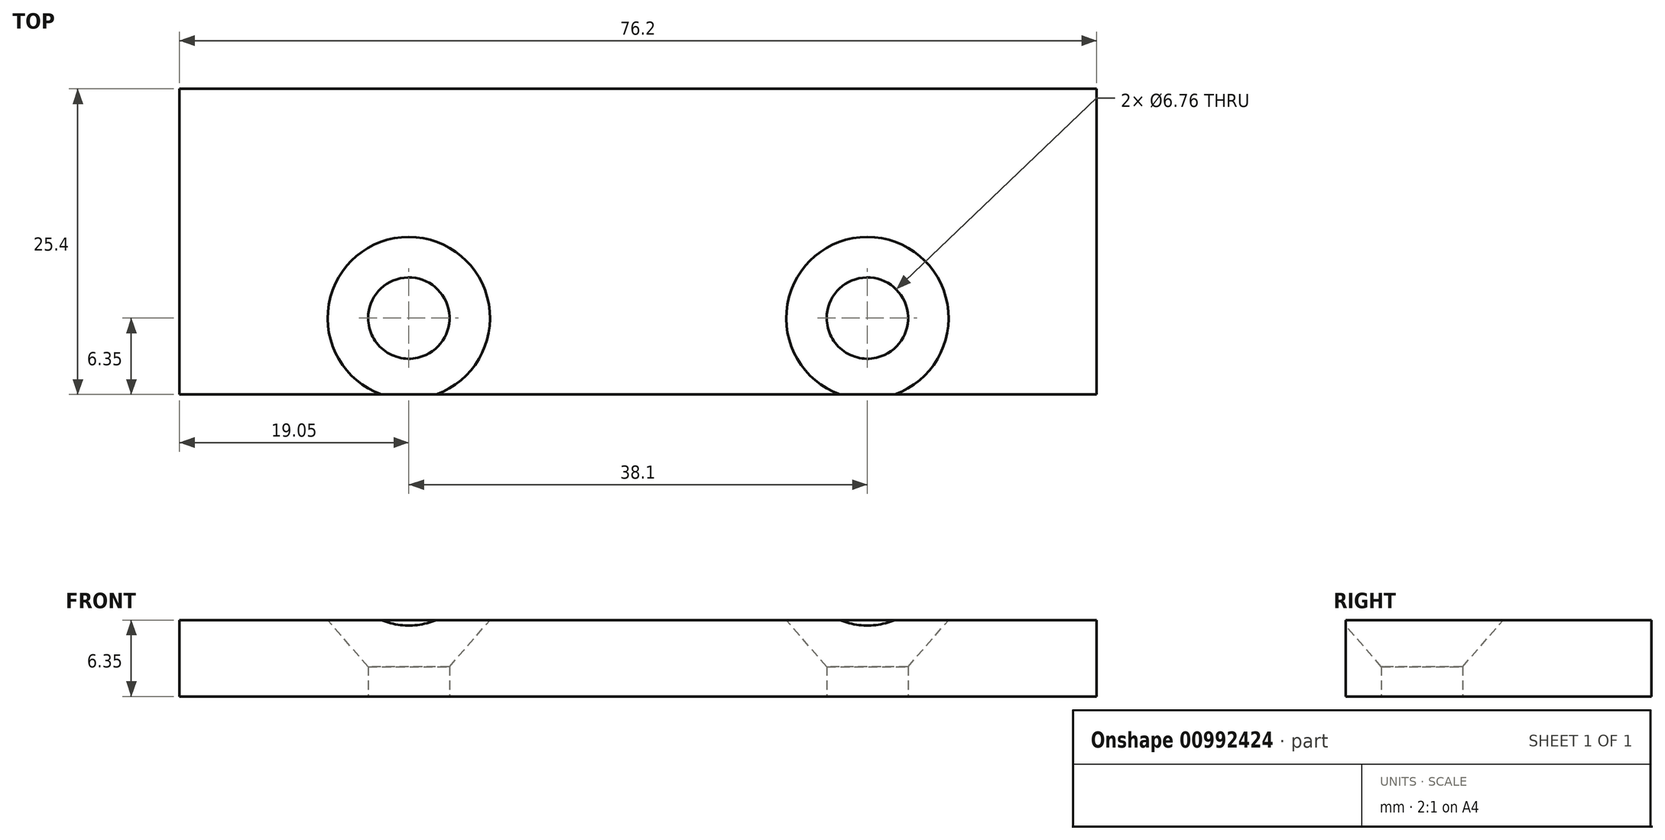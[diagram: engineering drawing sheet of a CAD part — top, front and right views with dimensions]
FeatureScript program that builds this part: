
annotation { "Feature Type Name" : "Feature", "Feature Type Description" : "" }
export const myFeature = defineFeature(function(context is Context, id is Id, definition is map)
    precondition{}
    {
        {
            var Q0;
            Q0=qCreatedBy(makeId("Top.planeOp"),FACE);
            var sketch = newSketch(context, id + "F0", { "sketchPlane" : qUnion([Q0])});
            skLineSegment(sketch, "E0.bottom", {"start": v(38.1, 12.7) * mm, "end": v(-38.1, 12.7) * mm});
            skLineSegment(sketch, "E0.top", {"start": v(38.1, -12.7) * mm, "end": v(-38.1, -12.7) * mm});
            skLineSegment(sketch, "E0.left", {"start": v(38.1, 12.7) * mm, "end": v(38.1, -12.7) * mm});
            skLineSegment(sketch, "E0.right", {"start": v(-38.1, 12.7) * mm, "end": v(-38.1, -12.7) * mm});
            skPoint(sketch, "E0.middle", {"position": v(0, 0) * mm});
            skCircle(sketch, "E1", {"center": v(-19.05, -6.35) * mm, "radius": 3.57 * mm});
            skCircle(sketch, "E2", {"center": v(19.05, -6.35) * mm, "radius": 3.57 * mm});
            skSolve(sketch);
        }
        {
            var Q0;
            Q0=makeQuery(id+"F0.imprint","IMPRINT",FACE,{"disambiguationData":[TD([[makeQuery(id+"F0.imprint","IMPRINT",EDGE,{"derivedFrom":sQuery(id+"F0.wireOp",EDGE,"E0.bottom")}),1.0]])]});
            var Q1;
            Q1=makeQuery(id+"F0.imprint","IMPRINT",FACE,{"disambiguationData":[TD([[makeQuery(id+"F0.imprint","IMPRINT",EDGE,{"derivedFrom":sQuery(id+"F0.wireOp",EDGE,"E2")}),1.0]])]});
            var Q2;
            Q2=makeQuery(id+"F0.imprint","IMPRINT",FACE,{"disambiguationData":[TD([[makeQuery(id+"F0.imprint","IMPRINT",EDGE,{"derivedFrom":sQuery(id+"F0.wireOp",EDGE,"E1")}),1.0]])]});
            extrude(context, id + "F1", {"entities" : qUnion([Q0, Q1, Q2]), "oppositeDirection" : true, "depth" : 6.35 * mm, "offsetDistance" : 25.4 * mm});
        }
        {
            var Q0;
            Q0=sQuery(id+"F0.wireOp",VERTEX,"E1.center");
            var Q1;
            Q1=sQuery(id+"F0.wireOp",VERTEX,"E2.center");
            var Q2;
            Q2=makeQuery(id+"F1.opExtrude","SWEPT_BODY",BODY,{"disambiguationData":[OSD([sQuery(id+"F0.wireOp",EDGE,"E0.bottom"),sQuery(id+"F0.wireOp",EDGE,"E0.top"),sQuery(id+"F0.wireOp",EDGE,"E0.left"),sQuery(id+"F0.wireOp",EDGE,"E0.right")])]});
            hole(context, id + "F2", {"style" : HoleStyle.C_SINK, "endStyle" : HoleEndStyle.BLIND, "standardTappedOrClearance" : lookupTablePath({ "fit" : "Close (ASME)", "standard" : "ANSI", "size" : "1/4", "type" : "Clearance" }), "standardBlindInLast" : lookupTablePath({ "fit" : "Close", "standard" : "ANSI", "engagement" : "75%", "pitch" : "20 tpi", "size" : "1/4", "type" : "Clearance & tapped" }), "holeDiameter" : 6.76 * mm, "cSinkDiameter" : 13.5 * mm, "cSinkAngle" : 82 * degree, "majorDiameter" : 6.35 * mm, "holeDepth" : 19.05 * mm, "isTappedThrough" : true, "tappedDepth" : 12.7 * mm, "tapClearance" : 3, "locations" : qUnion([Q0, Q1]), "scope" : qUnion([Q2]), "startStyle" : HoleStartStyle.SKETCH});
        }
    });
